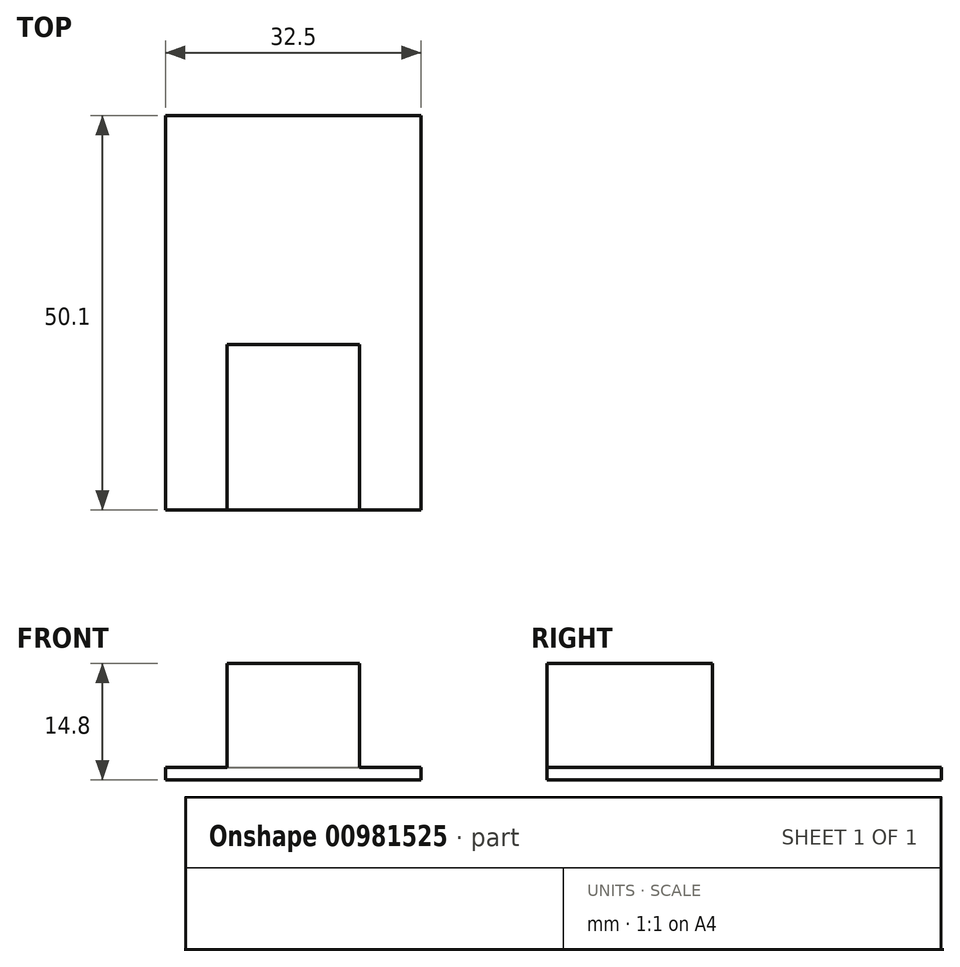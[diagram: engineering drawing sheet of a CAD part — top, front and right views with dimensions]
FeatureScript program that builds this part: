
annotation { "Feature Type Name" : "Feature", "Feature Type Description" : "" }
export const myFeature = defineFeature(function(context is Context, id is Id, definition is map)
    precondition{}
    {
        {
            var Q0;
            Q0=qCreatedBy(makeId("Top.planeOp"),FACE);
            var sketch = newSketch(context, id + "F0", { "sketchPlane" : qUnion([Q0])});
            skLineSegment(sketch, "E0.bottom", {"start": v(-16.25, 25.05) * mm, "end": v(16.25, 25.05) * mm});
            skLineSegment(sketch, "E0.top", {"start": v(-16.25, -25.05) * mm, "end": v(16.25, -25.05) * mm});
            skLineSegment(sketch, "E0.left", {"start": v(-16.25, 25.05) * mm, "end": v(-16.25, -25.05) * mm});
            skLineSegment(sketch, "E0.right", {"start": v(16.25, 25.05) * mm, "end": v(16.25, -25.05) * mm});
            skPoint(sketch, "E0.middle", {"position": v(0, 0) * mm});
            skSolve(sketch);
        }
        {
            var Q0;
            Q0=qCreatedBy(makeId("Front.planeOp"),FACE);
            var sketch = newSketch(context, id + "F1", { "sketchPlane" : qUnion([Q0])});
            skLineSegment(sketch, "E1.bottom", {"start": v(-8.4, 0) * mm, "end": v(8.4, 0) * mm});
            skLineSegment(sketch, "E1.top", {"start": v(-8.4, 13.2) * mm, "end": v(8.4, 13.2) * mm});
            skLineSegment(sketch, "E1.left", {"start": v(-8.4, 0) * mm, "end": v(-8.4, 13.2) * mm});
            skLineSegment(sketch, "E1.right", {"start": v(8.4, 0) * mm, "end": v(8.4, 13.2) * mm});
            skSolve(sketch);
        }
        {
            var Q0;
            Q0=makeQuery(id+"F0.imprint","IMPRINT",FACE,{"disambiguationData":[TD([[makeQuery(id+"F0.imprint","IMPRINT",EDGE,{"derivedFrom":sQuery(id+"F0.wireOp",EDGE,"E0.bottom")}),-1.0]])]});
            extrude(context, id + "F2", {"entities" : qUnion([Q0]), "oppositeDirection" : true, "depth" : 1.6 * mm, "offsetDistance" : 25 * mm});
        }
        {
            var Q0;
            Q0 = qSketchRegion(id + "F1", true);
            extrude(context, id + "F3", {"entities" : qUnion([Q0]), "operationType" : NewBodyOperationType.ADD, "depth" : 25.05 * mm, "offsetDistance" : 25 * mm, "hasSecondDirection" : true, "secondDirectionOppositeDirection" : false, "secondDirectionDepth" : 4.05 * mm});
        }
    });
